# Revit family: wash basin (318)
name_source: partatom
category: Plumbing Fixtures
units: mm (PartAtom-declared; Revit-internal decimal feet)

## family parameters
Always vertical = No
Cut with Voids When Loaded = No
OmniClass Number = 23.45.00.00
OmniClass Title = Sanitary, Laundry, and Cleaning Equipment
Part Type = Normal
Room Calculation Point = No
Round Connector Dimension = Use Diameter
Shared = No
Work Plane-Based = No

## types (1)
- Default
    BIMobject category = Toilet Accessories
    BIMobject category code = sanitary-toilet-accessories
    BIMobject main category = Sanitary
    BIMobject main category code = sanitary
    BOSUseNativeGeometries = 1
    Brand url = http://www.ceramicadolomite.it
    Default Elevation = 0' - 0"
    EAN code = https://8023246249400, 8023246249516, 8023246249417, 8023246249394
    Edition number = 1
    IFC Classification = Sanitary Terminal
    Installation instructions = http://www.idealstandard.it
    Manufacturer name = Ceramica Dolomite
    Masterformat 2014 Code = 12 30 00
    Masterformat 2014 Description = Casework
    NBS Reference Code = 35-75-10
    NBS Reference Description = Bathroom Integrated Ductwork
    OmniClass Code = 23-21 19 00
    OmniClass Description = Casework
    Product Guid = 7df0b90b-dfe6-4c73-a766-cf77caeda441
    Product SKU = J5273
    Product certification = http://www.idealstandard.it
    Product data url = https://bimobject.com
    Product family = Sanitary
    Product group = bathroom furniture
    Product name = GEMMA 2 VANITY 81.5 SDY GRY BSE 80 2 DRS
    Product url = http://www.idealstandard.it
    QR code = http://bimobject.com
    Technical description = http://www.idealstandard.it
    Uniclass 1.4 Code = L8241
    Uniclass 1.4 Description = Bathroom cabinets
    Uniclass 2.0 Code = PR-35-75-10
    Uniclass 2.0 Description = Bathroom Integrated Ductwork

## geometry (parser evidence)
native form markers: Sweep x2
no freeform markers — native parametric forms only
